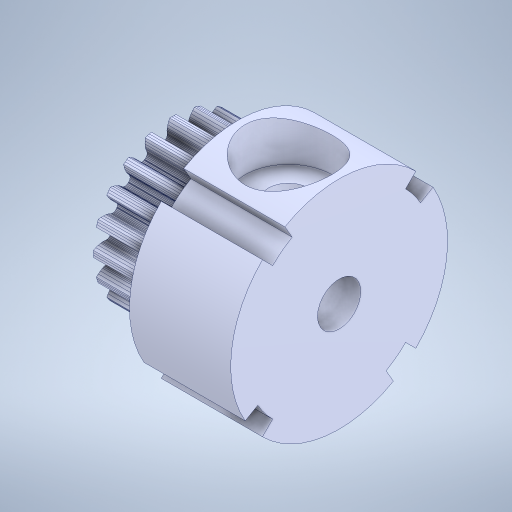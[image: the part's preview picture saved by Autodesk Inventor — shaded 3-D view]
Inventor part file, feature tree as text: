
AUTODESK INVENTOR PART (.ipt)
format: ipt  version: 2023.5 (Build 275446000, 446)  size: 2,189,312 bytes
history: native  units: mm
features: sketch x7, extrude x5, other x4, projected_geometry x3, pattern_circular x1, hole x1, mirror x1
ambient origin geometry x8: Origin, YZ Plane, XZ Plane, XY Plane, X Axis, Y Axis, Z Axis, Center Point
bodies: Body1 (feature_tree)
feature tree (22):
  extrude  "Wyciągnięcie proste1"  Depth=15.0mm
  extrude  "Wyciągnięcie proste2"  Depth=7.0mm TaperAngle=0.0deg
  sketch  "Szkic3"
  other  "Płaszczyzna konstrukcyjna2"
  extrude  "Wyciągnięcie proste3"  Depth=1.0mm TaperAngle=0.0deg
  pattern_circular  "Szyk kołowy1"  [2 undecoded]
  extrude  "Wyciągnięcie proste4"  TaperAngle=15.0deg  [1 undecoded]
  hole  "Otwór1"  [1 undecoded]
  mirror  "Odbij1"
  extrude  "Wyciągnięcie proste5"  TaperAngle=0.0deg  [1 undecoded]
  other  "Bryła31"
  sketch  "Szkic1"
  sketch  "Szkic2"
  projected_geometry  "Pętla rzutowana1"
  other  "Płaszczyzna konstrukcyjna1"
  sketch  "Szkic5"
  sketch  "Szkic6"
  projected_geometry  "Pętla rzutowana2"
  sketch  "Szkic7"
  sketch  "Szkic8"
  projected_geometry  "Pętla rzutowana3"
  other  "Engrane_8:1"
note: 5 required parameter values undecoded (feature->parameter linkage not recoverable at this tier; creation-order binding heuristic only, values carry confidence <= 0.55)
